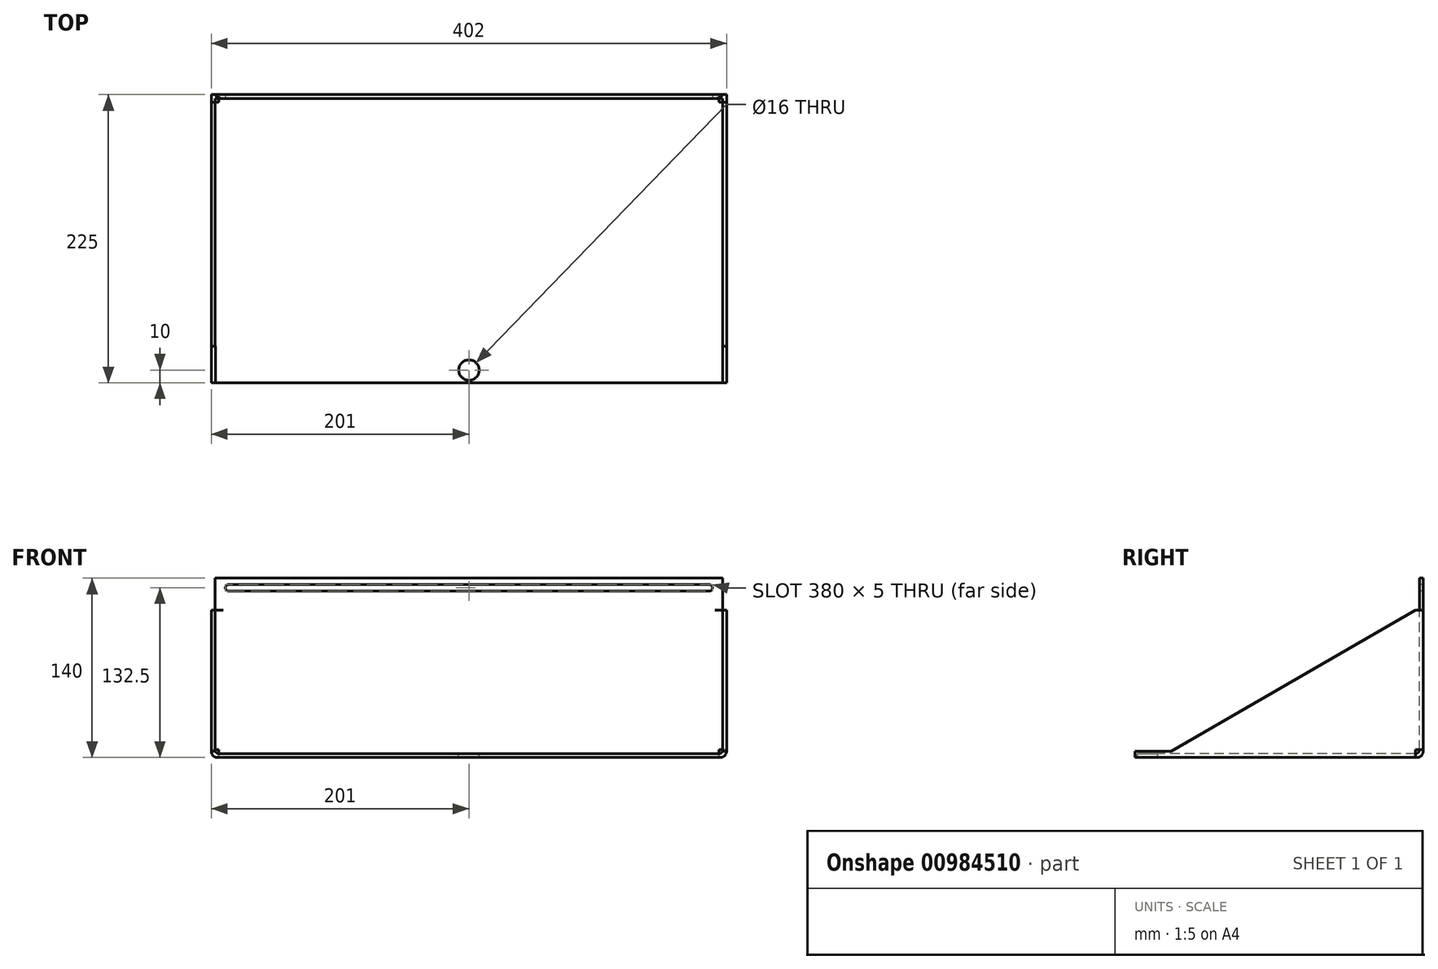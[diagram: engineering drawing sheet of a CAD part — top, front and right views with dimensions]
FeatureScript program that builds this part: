
annotation { "Feature Type Name" : "Feature", "Feature Type Description" : "" }
export const myFeature = defineFeature(function(context is Context, id is Id, definition is map)
    precondition{}
    {
        {
            var Q0;
            Q0=qCreatedBy(makeId("Right.planeOp"),FACE);
            var sketch = newSketch(context, id + "F0", { "sketchPlane" : qUnion([Q0])});
            skLineSegment(sketch, "E0", {"start": v(0, 3) * mm, "end": v(222, 3) * mm});
            skLineSegment(sketch, "E1", {"start": v(222, 3) * mm, "end": v(222, 140) * mm});
            skLineSegment(sketch, "E2", {"start": v(222, 140) * mm, "end": v(225, 140) * mm});
            skLineSegment(sketch, "E3", {"start": v(225, 140) * mm, "end": v(225, 0) * mm});
            skLineSegment(sketch, "E4", {"start": v(225, 0) * mm, "end": v(0, 0) * mm});
            skLineSegment(sketch, "E5", {"start": v(0, 0) * mm, "end": v(0, 3) * mm});
            skSolve(sketch);
        }
        {
            var Q0;
            Q0 = qSketchRegion(id + "F0", true);
            extrude(context, id + "F1", {"entities" : qUnion([Q0]), "depth" : 195 * mm, "offsetDistance" : 25 * mm, "hasSecondDirection" : true, "secondDirectionOppositeDirection" : true, "secondDirectionDepth" : 195 * mm});
        }
        {
            var Q0;
            Q0=makeQuery(id+"F1.opExtrude","SWEPT_EDGE",EDGE,{"disambiguationData":[OSD([sQuery(id+"F0.wireOp",EDGE,"E0"),sQuery(id+"F0.wireOp",EDGE,"E1")])]});
            fillet(context, id + "F2", {"entities" : qUnion([Q0]), "radius" : 3 * mm, "tangentPropagation" : true, "allowEdgeOverflow" : false});
        }
        {
            var Q0;
            Q0=makeQuery(id+"F1.opExtrude","SWEPT_EDGE",EDGE,{"disambiguationData":[OSD([sQuery(id+"F0.wireOp",EDGE,"E3"),sQuery(id+"F0.wireOp",EDGE,"E4")])]});
            fillet(context, id + "F3", {"entities" : qUnion([Q0]), "radius" : 5 * mm, "tangentPropagation" : true, "allowEdgeOverflow" : false});
        }
        {
            var Q0;
            Q0=qCreatedBy(makeId("Front.planeOp"),FACE);
            var sketch = newSketch(context, id + "F4", { "sketchPlane" : qUnion([Q0])});
            skLineSegment(sketch, "E6", {"start": v(0, 0) * mm, "end": v(-201, 0) * mm});
            skLineSegment(sketch, "E7", {"start": v(-201, 0) * mm, "end": v(-201, 135) * mm});
            skLineSegment(sketch, "E8", {"start": v(-201, 135) * mm, "end": v(-198, 135) * mm});
            skLineSegment(sketch, "E9", {"start": v(-198, 135) * mm, "end": v(-198, 3) * mm});
            skLineSegment(sketch, "E10", {"start": v(-198, 3) * mm, "end": v(198, 3) * mm});
            skLineSegment(sketch, "E11", {"start": v(198, 3) * mm, "end": v(198, 135) * mm});
            skLineSegment(sketch, "E12", {"start": v(198, 135) * mm, "end": v(201, 135) * mm});
            skLineSegment(sketch, "E13", {"start": v(201, 135) * mm, "end": v(201, 0) * mm});
            skLineSegment(sketch, "E14", {"start": v(201, 0) * mm, "end": v(0, 0) * mm});
            skSolve(sketch);
        }
        {
            var Q0;
            Q0 = qSketchRegion(id + "F4", true);
            extrude(context, id + "F5", {"entities" : qUnion([Q0]), "operationType" : NewBodyOperationType.ADD, "oppositeDirection" : true, "depth" : 219 * mm, "offsetDistance" : 25 * mm});
        }
        {
            var Q0;
            Q0=makeQuery(id+"F5.opExtrude","SWEPT_EDGE",EDGE,{"disambiguationData":[OSD([sQuery(id+"F4.wireOp",EDGE,"E9"),sQuery(id+"F4.wireOp",EDGE,"E10")])]});
            var Q1;
            Q1=makeQuery(id+"F5.opExtrude","SWEPT_EDGE",EDGE,{"disambiguationData":[OSD([sQuery(id+"F4.wireOp",EDGE,"E10"),sQuery(id+"F4.wireOp",EDGE,"E11")])]});
            fillet(context, id + "F6", {"entities" : qUnion([Q0, Q1]), "radius" : 3 * mm, "tangentPropagation" : true, "allowEdgeOverflow" : false});
        }
        {
            var Q0;
            Q0=makeQuery(id+"F5.opExtrude","SWEPT_EDGE",EDGE,{"disambiguationData":[OSD([sQuery(id+"F4.wireOp",EDGE,"E6"),sQuery(id+"F4.wireOp",EDGE,"E7")])]});
            var Q1;
            Q1=makeQuery(id+"F5.opExtrude","SWEPT_EDGE",EDGE,{"disambiguationData":[OSD([sQuery(id+"F4.wireOp",EDGE,"E13"),sQuery(id+"F4.wireOp",EDGE,"E14")])]});
            fillet(context, id + "F7", {"entities" : qUnion([Q0, Q1]), "radius" : 5 * mm, "tangentPropagation" : true, "allowEdgeOverflow" : false});
        }
        {
            var Q0;
            Q0=makeQuery(id+"F5.opExtrude","SWEPT_FACE",FACE,{"disambiguationData":[OSD([sQuery(id+"F4.wireOp",EDGE,"E7")])]});
            var sketch = newSketch(context, id + "F8", { "sketchPlane" : qUnion([Q0])});
            skLineSegment(sketch, "E15", {"start": v(-219, 115) * mm, "end": v(-28.47, 5) * mm});
            skLineSegment(sketch, "E16", {"start": v(-28.47, 5) * mm, "end": v(0, 5) * mm});
            skLineSegment(sketch, "E17", {"start": v(0, 5) * mm, "end": v(0, 135) * mm});
            skLineSegment(sketch, "E18", {"start": v(0, 135) * mm, "end": v(-219, 135) * mm});
            skLineSegment(sketch, "E19", {"start": v(-219, 135) * mm, "end": v(-219, 115) * mm});
            skSolve(sketch);
        }
        {
            var Q0;
            Q0 = qSketchRegion(id + "F8", true);
            extrude(context, id + "F9", {"entities" : qUnion([Q0]), "operationType" : NewBodyOperationType.REMOVE, "endBound" : BoundingType.THROUGH_ALL, "oppositeDirection" : true, "depth" : 25 * mm, "offsetDistance" : 25 * mm});
        }
        {
            var Q0;
            Q0=makeQuery(id+"F5.boolean.opBoolean","MERGE",FACE,{"derivedFrom":[makeQuery(id+"F1.opExtrude","SWEPT_FACE",FACE,{"disambiguationData":[OSD([sQuery(id+"F0.wireOp",EDGE,"E0")])]}),makeQuery(id+"F5.opExtrude","SWEPT_FACE",FACE,{"disambiguationData":[OSD([sQuery(id+"F4.wireOp",EDGE,"E10")])]})]});
            var sketch = newSketch(context, id + "F10", { "sketchPlane" : qUnion([Q0])});
            skCircle(sketch, "E20", {"center": v(0, 10) * mm, "radius": 8 * mm});
            skSolve(sketch);
        }
        {
            var Q0;
            Q0 = qSketchRegion(id + "F10", true);
            extrude(context, id + "F11", {"entities" : qUnion([Q0]), "operationType" : NewBodyOperationType.REMOVE, "oppositeDirection" : true, "depth" : 3 * mm, "offsetDistance" : 25 * mm});
        }
        {
            var Q0;
            Q0=makeQuery(id+"F1.opExtrude","SWEPT_FACE",FACE,{"disambiguationData":[OSD([sQuery(id+"F0.wireOp",EDGE,"E1")])]});
            var sketch = newSketch(context, id + "F12", { "sketchPlane" : qUnion([Q0])});
            skLineSegment(sketch, "E21", {"start": v(-187.5, 135) * mm, "end": v(187.5, 135) * mm});
            skLineSegment(sketch, "E22", {"start": v(187.5, 130) * mm, "end": v(-187.5, 130) * mm});
            skArc(sketch, "E23", {"start": v(-187.5, 135) * mm, "mid": v(-190, 132.5) * mm, "end": v(-187.5, 130) * mm});
            skArc(sketch, "E24", {"start": v(187.5, 130) * mm, "mid": v(190, 132.5) * mm, "end": v(187.5, 135) * mm});
            skSolve(sketch);
        }
        {
            var Q0;
            Q0 = qSketchRegion(id + "F12", true);
            extrude(context, id + "F13", {"entities" : qUnion([Q0]), "operationType" : NewBodyOperationType.REMOVE, "oppositeDirection" : true, "depth" : 3 * mm, "offsetDistance" : 25 * mm});
        }
        {
            var Q0;
            {var subQ2=sQuery(id+"F4.wireOp",EDGE,"E10");var subQ4=sQuery(id+"F4.wireOp",EDGE,"E7");var subQ5=sQuery(id+"F4.wireOp",EDGE,"E14");var subQ6=sQuery(id+"F4.wireOp",EDGE,"E6");var subQ7=sQuery(id+"F4.wireOp",EDGE,"E8");var subQ8=sQuery(id+"F4.wireOp",EDGE,"E9");Q0=makeQuery(id+"F5.boolean.opBoolean","SPLIT",FACE,{"disambiguationData":[TD([makeQuery(id+"F5.opExtrude","SWEPT_FACE",FACE,{"disambiguationData":[OSD([subQ4])]})])],"derivedFrom":makeQuery(id+"F5.opExtrude","CAP_FACE",FACE,{"disambiguationData":[OSD([subQ6,subQ4,subQ7,subQ8,subQ2,sQuery(id+"F4.wireOp",EDGE,"E11"),sQuery(id+"F4.wireOp",EDGE,"E12"),sQuery(id+"F4.wireOp",EDGE,"E13"),subQ5])],"isStart":false})});}
            var sketch = newSketch(context, id + "F14", { "sketchPlane" : qUnion([Q0])});
            skLineSegment(sketch, "E25.bottom", {"start": v(-201, 115) * mm, "end": v(-198, 115) * mm});
            skLineSegment(sketch, "E25.top", {"start": v(-201, 6) * mm, "end": v(-198, 6) * mm});
            skLineSegment(sketch, "E25.left", {"start": v(-201, 115) * mm, "end": v(-201, 6) * mm});
            skLineSegment(sketch, "E25.right", {"start": v(-198, 115) * mm, "end": v(-198, 6) * mm});
            skLineSegment(sketch, "E26.MirrorCS", {"start": v(201, 115) * mm, "end": v(201, 6) * mm});
            skLineSegment(sketch, "E27.MirrorCS", {"start": v(198, 115) * mm, "end": v(198, 6) * mm});
            skLineSegment(sketch, "E28.MirrorCS", {"start": v(201, 6) * mm, "end": v(198, 6) * mm});
            skLineSegment(sketch, "E29.MirrorCS", {"start": v(201, 115) * mm, "end": v(198, 115) * mm});
            skSolve(sketch);
        }
        {
            var Q0;
            Q0 = qSketchRegion(id + "F14", true);
            extrude(context, id + "F15", {"entities" : qUnion([Q0]), "operationType" : NewBodyOperationType.ADD, "depth" : 6 * mm, "offsetDistance" : 25 * mm});
        }
        {
            var Q0;
            Q0=makeQuery(id+"F1.opExtrude","CAP_FACE",FACE,{"disambiguationData":[OSD([sQuery(id+"F0.wireOp",EDGE,"E0"),sQuery(id+"F0.wireOp",EDGE,"E1"),sQuery(id+"F0.wireOp",EDGE,"E2"),sQuery(id+"F0.wireOp",EDGE,"E3"),sQuery(id+"F0.wireOp",EDGE,"E4"),sQuery(id+"F0.wireOp",EDGE,"E5")])],"isStart":false});
            var sketch = newSketch(context, id + "F16", { "sketchPlane" : qUnion([Q0])});
            skLineSegment(sketch, "E30.bottom", {"start": v(225, 140) * mm, "end": v(222, 140) * mm});
            skLineSegment(sketch, "E30.top", {"start": v(225, 6) * mm, "end": v(222, 6) * mm});
            skLineSegment(sketch, "E30.left", {"start": v(225, 140) * mm, "end": v(225, 6) * mm});
            skLineSegment(sketch, "E30.right", {"start": v(222, 140) * mm, "end": v(222, 6) * mm});
            skSolve(sketch);
        }
        {
            var Q0;
            Q0 = qSketchRegion(id + "F16", true);
            extrude(context, id + "F17", {"entities" : qUnion([Q0]), "operationType" : NewBodyOperationType.ADD, "depth" : 3 * mm, "offsetDistance" : 25 * mm});
        }
        {
            var Q0;
            Q0=makeQuery(id+"F1.opExtrude","CAP_FACE",FACE,{"disambiguationData":[OSD([sQuery(id+"F0.wireOp",EDGE,"E0"),sQuery(id+"F0.wireOp",EDGE,"E1"),sQuery(id+"F0.wireOp",EDGE,"E2"),sQuery(id+"F0.wireOp",EDGE,"E3"),sQuery(id+"F0.wireOp",EDGE,"E4"),sQuery(id+"F0.wireOp",EDGE,"E5")])],"isStart":true});
            var sketch = newSketch(context, id + "F18", { "sketchPlane" : qUnion([Q0])});
            skLineSegment(sketch, "E31.bottom", {"start": v(-225, 140) * mm, "end": v(-222, 140) * mm});
            skLineSegment(sketch, "E31.top", {"start": v(-225, 6) * mm, "end": v(-222, 6) * mm});
            skLineSegment(sketch, "E31.left", {"start": v(-225, 140) * mm, "end": v(-225, 6) * mm});
            skLineSegment(sketch, "E31.right", {"start": v(-222, 140) * mm, "end": v(-222, 6) * mm});
            skSolve(sketch);
        }
        {
            var Q0;
            Q0 = qSketchRegion(id + "F18", true);
            extrude(context, id + "F19", {"entities" : qUnion([Q0]), "operationType" : NewBodyOperationType.ADD, "depth" : 3 * mm, "offsetDistance" : 25 * mm});
        }
        {
            var Q0;
            {var subQ0=sQuery(id+"F16.wireOp",EDGE,"E30.right");Q0=makeQuery(id+"F17.boolean.opBoolean","SPLIT",EDGE,{"disambiguationData":[topologyDisambiguationEdgeConnected([makeQuery(id+"F5.opExtrude","SWEPT_FACE",FACE,{"disambiguationData":[OSD([sQuery(id+"F4.wireOp",EDGE,"E11")])]})])],"derivedFrom":makeQuery(id+"F17.opExtrude","CAP_EDGE",EDGE,{"disambiguationData":[OSD([subQ0])],"isStart":false})});}
            var Q1;
            {var subQ0=sQuery(id+"F18.wireOp",EDGE,"E31.right");Q1=makeQuery(id+"F19.boolean.opBoolean","SPLIT",EDGE,{"disambiguationData":[topologyDisambiguationEdgeConnected([makeQuery(id+"F5.opExtrude","SWEPT_FACE",FACE,{"disambiguationData":[OSD([sQuery(id+"F4.wireOp",EDGE,"E9")])]})])],"derivedFrom":makeQuery(id+"F19.opExtrude","CAP_EDGE",EDGE,{"disambiguationData":[OSD([subQ0])],"isStart":false})});}
            fillet(context, id + "F20", {"entities" : qUnion([Q0, Q1]), "radius" : 8 * mm, "tangentPropagation" : true, "allowEdgeOverflow" : false});
        }
    });
